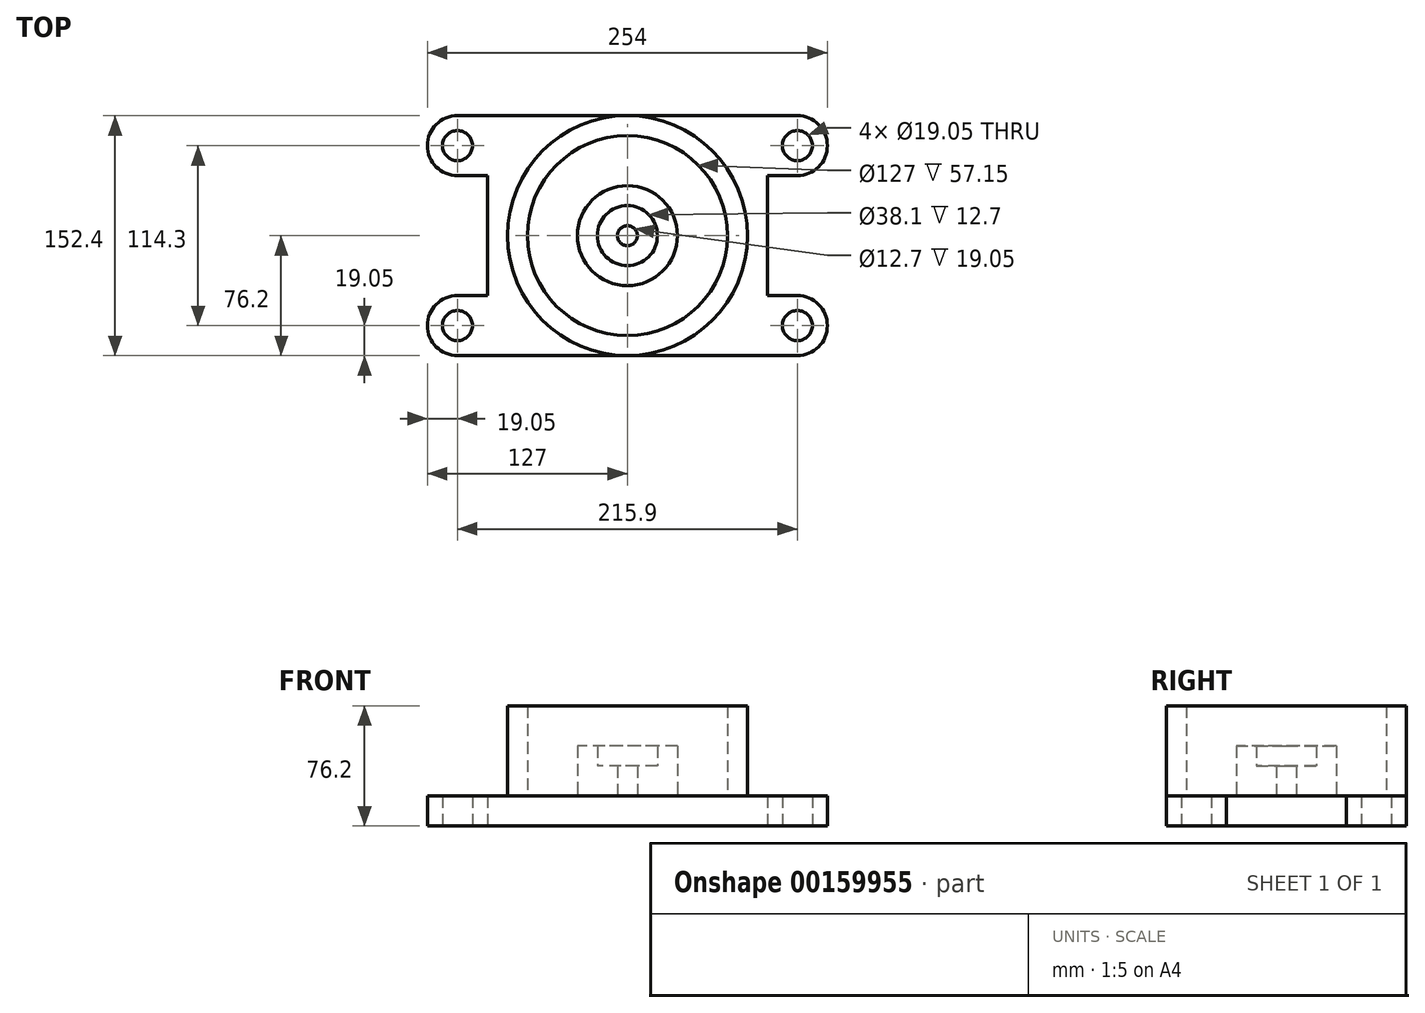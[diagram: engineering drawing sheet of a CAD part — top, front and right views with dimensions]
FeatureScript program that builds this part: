
annotation { "Feature Type Name" : "Feature", "Feature Type Description" : "" }
export const myFeature = defineFeature(function(context is Context, id is Id, definition is map)
    precondition{}
    {
        {
            var Q0;
            Q0=qCreatedBy(makeId("Top.planeOp"),FACE);
            var sketch = newSketch(context, id + "F0", { "sketchPlane" : qUnion([Q0])});
            skCircle(sketch, "E0", {"center": v(0, 0) * mm, "radius": 76.2 * mm});
            skCircle(sketch, "E1", {"center": v(0, 0) * mm, "radius": 63.5 * mm});
            skCircle(sketch, "E2", {"center": v(0, 0) * mm, "radius": 31.75 * mm});
            skCircle(sketch, "E3", {"center": v(0, 0) * mm, "radius": 19.05 * mm});
            skCircle(sketch, "E4", {"center": v(0, 0) * mm, "radius": 6.35 * mm});
            skLineSegment(sketch, "E5.bottom", {"start": v(-88.9, 76.2) * mm, "end": v(88.9, 76.2) * mm});
            skLineSegment(sketch, "E5.top", {"start": v(-88.9, -76.2) * mm, "end": v(88.9, -76.2) * mm});
            skLineSegment(sketch, "E5.left", {"start": v(-88.9, 38.1) * mm, "end": v(-88.9, -38.1) * mm});
            skCircle(sketch, "E6", {"center": v(-107.95, -57.15) * mm, "radius": 9.53 * mm});
            skArc(sketch, "E7", {"start": v(-107.95, -38.1) * mm, "mid": v(-127, -57.15) * mm, "end": v(-107.95, -76.2) * mm});
            skLineSegment(sketch, "E8", {"start": v(0, 0) * mm, "end": v(0, -76.2) * mm, "construction": true});
            skLineSegment(sketch, "E9", {"start": v(0, 0) * mm, "end": v(88.9, 0) * mm, "construction": true});
            skCircle(sketch, "E10.MirrorC", {"center": v(107.95, -57.15) * mm, "radius": 9.53 * mm});
            skArc(sketch, "E11.MirrorC", {"start": v(107.95, -38.1) * mm, "mid": v(127, -57.15) * mm, "end": v(107.95, -76.2) * mm});
            skArc(sketch, "E12.MirrorC", {"start": v(-107.95, 38.1) * mm, "mid": v(-127, 57.15) * mm, "end": v(-107.95, 76.2) * mm});
            skCircle(sketch, "E13.MirrorC", {"center": v(-107.95, 57.15) * mm, "radius": 9.53 * mm});
            skArc(sketch, "E14.MirrorC", {"start": v(107.95, 38.1) * mm, "mid": v(127, 57.15) * mm, "end": v(107.95, 76.2) * mm});
            skCircle(sketch, "E15.MirrorC", {"center": v(107.95, 57.15) * mm, "radius": 9.53 * mm});
            skLineSegment(sketch, "E16", {"start": v(-88.9, 76.2) * mm, "end": v(-107.95, 76.2) * mm});
            skLineSegment(sketch, "E17", {"start": v(-88.9, -76.2) * mm, "end": v(-107.95, -76.2) * mm});
            skLineSegment(sketch, "E18.MirrorCS", {"start": v(88.9, -76.2) * mm, "end": v(107.95, -76.2) * mm});
            skLineSegment(sketch, "E19.MirrorCS", {"start": v(88.9, 76.2) * mm, "end": v(107.95, 76.2) * mm});
            skLineSegment(sketch, "E20", {"start": v(-107.95, 38.1) * mm, "end": v(-88.9, 38.1) * mm});
            skLineSegment(sketch, "E21.MirrorCS", {"start": v(107.95, 38.1) * mm, "end": v(88.9, 38.1) * mm});
            skLineSegment(sketch, "E22.MirrorCS", {"start": v(107.95, -38.1) * mm, "end": v(88.9, -38.1) * mm});
            skLineSegment(sketch, "E23.MirrorCS", {"start": v(-107.95, -38.1) * mm, "end": v(-88.9, -38.1) * mm});
            skLineSegment(sketch, "E24.trimOffspring", {"start": v(88.9, 38.1) * mm, "end": v(88.9, -38.1) * mm});
            skSolve(sketch);
        }
        {
            var Q0;
            Q0 = qSketchRegion(id + "F0", true);
            var Q1;
            Q1=makeQuery(id+"F0.imprint","IMPRINT",FACE,{"disambiguationData":[TD([[makeQuery(id+"F0.imprint","IMPRINT",EDGE,{"derivedFrom":sQuery(id+"F0.wireOp",EDGE,"E1")}),1.0]])]});
            var Q2;
            Q2=makeQuery(id+"F0.imprint","IMPRINT",FACE,{"disambiguationData":[TD([[makeQuery(id+"F0.imprint","IMPRINT",EDGE,{"derivedFrom":sQuery(id+"F0.wireOp",EDGE,"E2")}),1.0]])]});
            var Q3;
            Q3=makeQuery(id+"F0.imprint","IMPRINT",FACE,{"disambiguationData":[TD([[makeQuery(id+"F0.imprint","IMPRINT",EDGE,{"derivedFrom":sQuery(id+"F0.wireOp",EDGE,"E3")}),1.0]])]});
            var Q4;
            Q4=makeQuery(id+"F0.imprint","IMPRINT",FACE,{"disambiguationData":[TD([[makeQuery(id+"F0.imprint","IMPRINT",EDGE,{"derivedFrom":sQuery(id+"F0.wireOp",EDGE,"E4")}),1.0]])]});
            extrude(context, id + "F1", {"entities" : qUnion([Q0, Q1, Q2, Q3, Q4]), "depth" : 19.05 * mm});
        }
        {
            var Q0;
            Q0=makeQuery(id+"F0.imprint","IMPRINT",FACE,{"disambiguationData":[TD([[makeQuery(id+"F0.imprint","IMPRINT",EDGE,{"derivedFrom":sQuery(id+"F0.wireOp",EDGE,"E1")}),-1.0]])]});
            extrude(context, id + "F2", {"entities" : qUnion([Q0]), "operationType" : NewBodyOperationType.ADD, "depth" : 76.2 * mm});
        }
        {
            var Q0;
            Q0=makeQuery(id+"F0.imprint","IMPRINT",FACE,{"disambiguationData":[TD([[makeQuery(id+"F0.imprint","IMPRINT",EDGE,{"derivedFrom":sQuery(id+"F0.wireOp",EDGE,"E2")}),1.0]])]});
            extrude(context, id + "F3", {"entities" : qUnion([Q0]), "operationType" : NewBodyOperationType.ADD, "depth" : 50.8 * mm});
        }
        {
            var Q0;
            Q0=makeQuery(id+"F0.imprint","IMPRINT",FACE,{"disambiguationData":[TD([[makeQuery(id+"F0.imprint","IMPRINT",EDGE,{"derivedFrom":sQuery(id+"F0.wireOp",EDGE,"E3")}),1.0]])]});
            extrude(context, id + "F4", {"entities" : qUnion([Q0]), "operationType" : NewBodyOperationType.ADD, "depth" : 38.1 * mm});
        }
    });
